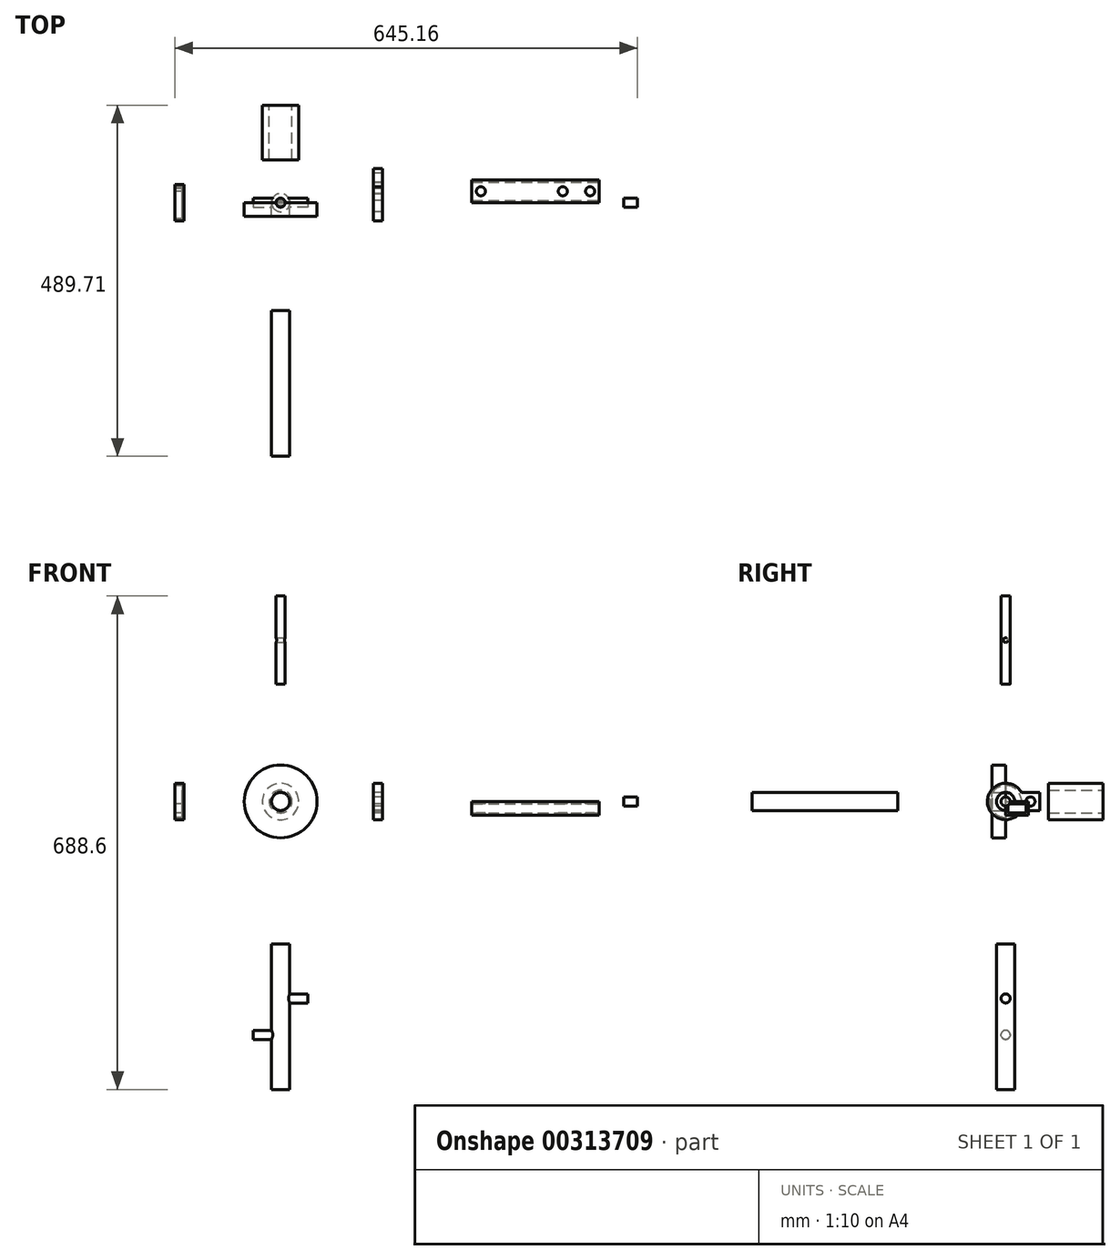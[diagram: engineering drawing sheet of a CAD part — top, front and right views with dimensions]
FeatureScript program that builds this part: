
annotation { "Feature Type Name" : "Feature", "Feature Type Description" : "" }
export const myFeature = defineFeature(function(context is Context, id is Id, definition is map)
    precondition{}
    {
        {
            var Q0;
            Q0=qCreatedBy(makeId("Front.planeOp"),FACE);
            var sketch = newSketch(context, id + "F0", { "sketchPlane" : qUnion([Q0])});
            skCircle(sketch, "E0", {"center": v(0, 0) * mm, "radius": 50.8 * mm});
            skCircle(sketch, "E1", {"center": v(0, 0) * mm, "radius": 12.7 * mm});
            skSolve(sketch);
        }
        {
            var Q0;
            Q0 = qSketchRegion(id + "F0", true);
            extrude(context, id + "F1", {"entities" : qUnion([Q0]), "depth" : 19.05 * mm});
        }
        {
            var Q0;
            Q0=qCreatedBy(makeId("Right.planeOp"),FACE);
            cPlane(context, id + "F2", {"entities" : qUnion([Q0]), "cplaneType" : CPlaneType.OFFSET, "offset" : 147.57 * mm, "oppositeDirection" : true, "width" : 152.4 * mm, "height" : 152.4 * mm});
        }
        {
            var Q0;
            Q0=qCreatedBy(id+"F2.planeOp",FACE);
            var sketch = newSketch(context, id + "F3", { "sketchPlane" : qUnion([Q0])});
            skCircle(sketch, "E2", {"center": v(0, 0) * mm, "radius": 25.4 * mm});
            skCircle(sketch, "E3", {"center": v(0, 0) * mm, "radius": 12.7 * mm});
            skSolve(sketch);
        }
        {
            var Q0;
            Q0 = qSketchRegion(id + "F3", true);
            extrude(context, id + "F4", {"entities" : qUnion([Q0]), "depth" : 12.7 * mm});
        }
        {
            var Q0;
            Q0=makeQuery(id+"F4.opExtrude","CAP_FACE",FACE,{"disambiguationData":[OSD([sQuery(id+"F3.wireOp",EDGE,"E2")])],"isStart":true});
            var sketch = newSketch(context, id + "F5", { "sketchPlane" : qUnion([Q0])});
            skCircle(sketch, "E4", {"center": v(0, 0) * mm, "radius": 22.22 * mm});
            skSolve(sketch);
        }
        {
            var Q0;
            Q0 = qSketchRegion(id + "F5", true);
            extrude(context, id + "F6", {"entities" : qUnion([Q0]), "operationType" : NewBodyOperationType.REMOVE, "oppositeDirection" : true, "depth" : 10.16 * mm});
        }
        {
            var Q0;
            Q0=qCreatedBy(makeId("Right.planeOp"),FACE);
            cPlane(context, id + "F7", {"entities" : qUnion([Q0]), "cplaneType" : CPlaneType.OFFSET, "offset" : 129.29 * mm, "width" : 152.4 * mm, "height" : 152.4 * mm});
        }
        {
            var Q0;
            Q0=qCreatedBy(id+"F7.planeOp",FACE);
            var sketch = newSketch(context, id + "F8", { "sketchPlane" : qUnion([Q0])});
            skCircle(sketch, "E5", {"center": v(0, 0) * mm, "radius": 25.4 * mm});
            skCircle(sketch, "E6", {"center": v(0, 0) * mm, "radius": 12.7 * mm});
            skLineSegment(sketch, "E7", {"start": v(0, 0) * mm, "end": v(52.55, 0) * mm, "construction": true});
            skLineSegment(sketch, "E8", {"start": v(22, 12.7) * mm, "end": v(47.4, 12.7) * mm});
            skLineSegment(sketch, "E9", {"start": v(47.4, 12.7) * mm, "end": v(47.4, 0) * mm});
            skLineSegment(sketch, "E10.MirrorCS", {"start": v(47.4, -12.7) * mm, "end": v(47.4, 0) * mm});
            skLineSegment(sketch, "E11.MirrorCS", {"start": v(22, -12.7) * mm, "end": v(47.4, -12.7) * mm});
            skCircle(sketch, "E12", {"center": v(34.7, 0) * mm, "radius": 6.35 * mm});
            skSolve(sketch);
        }
        {
            var Q0;
            Q0=makeQuery(id+"F8.imprint","IMPRINT",FACE,{"disambiguationData":[TD([[makeQuery(id+"F8.imprint","IMPRINT",EDGE,{"derivedFrom":sQuery(id+"F8.wireOp",EDGE,"E6")}),-1.0]])]});
            var Q1;
            {var subQ1=sQuery(id+"F8.wireOp",EDGE,"E8");Q1=makeQuery(id+"F8.imprint","IMPRINT",FACE,{"disambiguationData":[TD([[makeQuery(id+"F8.imprint","IMPRINT",EDGE,{"derivedFrom":subQ1}),-1.0]])]});}
            extrude(context, id + "F9", {"entities" : qUnion([Q0, Q1]), "depth" : 12.7 * mm});
        }
        {
            var Q0;
            Q0=qCreatedBy(makeId("Front.planeOp"),FACE);
            cPlane(context, id + "F10", {"entities" : qUnion([Q0]), "cplaneType" : CPlaneType.OFFSET, "offset" : 135.89 * mm, "oppositeDirection" : true, "width" : 152.4 * mm, "height" : 152.4 * mm});
        }
        {
            var Q0;
            Q0=qCreatedBy(id+"F10.planeOp",FACE);
            var sketch = newSketch(context, id + "F11", { "sketchPlane" : qUnion([Q0])});
            skCircle(sketch, "E13", {"center": v(0, 0) * mm, "radius": 25.4 * mm});
            skCircle(sketch, "E14", {"center": v(0, 0) * mm, "radius": 15.88 * mm});
            skSolve(sketch);
        }
        {
            var Q0;
            Q0 = qSketchRegion(id + "F11", true);
            extrude(context, id + "F12", {"entities" : qUnion([Q0]), "depth" : 76.2 * mm});
        }
        {
            var Q0;
            Q0=qCreatedBy(makeId("Front.planeOp"),FACE);
            cPlane(context, id + "F13", {"entities" : qUnion([Q0]), "cplaneType" : CPlaneType.OFFSET, "offset" : 150.62 * mm, "width" : 152.4 * mm, "height" : 152.4 * mm});
        }
        {
            var Q0;
            Q0=qCreatedBy(id+"F13.planeOp",FACE);
            var sketch = newSketch(context, id + "F14", { "sketchPlane" : qUnion([Q0])});
            skCircle(sketch, "E15", {"center": v(0, 0) * mm, "radius": 12.7 * mm});
            skSolve(sketch);
        }
        {
            var Q0;
            Q0 = qSketchRegion(id + "F14", true);
            extrude(context, id + "F15", {"entities" : qUnion([Q0]), "depth" : 203.2 * mm});
        }
        {
            var Q0;
            Q0=qCreatedBy(makeId("Top.planeOp"),FACE);
            cPlane(context, id + "F16", {"entities" : qUnion([Q0]), "cplaneType" : CPlaneType.OFFSET, "offset" : 163.58 * mm, "width" : 152.4 * mm, "height" : 152.4 * mm});
        }
        {
            var Q0;
            Q0=qCreatedBy(id+"F16.planeOp",FACE);
            var sketch = newSketch(context, id + "F17", { "sketchPlane" : qUnion([Q0])});
            skCircle(sketch, "E16", {"center": v(0, 0) * mm, "radius": 6.35 * mm});
            skSolve(sketch);
        }
        {
            var Q0;
            Q0 = qSketchRegion(id + "F17", true);
            extrude(context, id + "F18", {"entities" : qUnion([Q0]), "depth" : 123.19 * mm});
        }
        {
            var Q0;
            Q0=qCreatedBy(makeId("Right.planeOp"),FACE);
            var sketch = newSketch(context, id + "F19", { "sketchPlane" : qUnion([Q0])});
            skLineSegment(sketch, "E17", {"start": v(-6.35, 163.58) * mm, "end": v(-6.35, 286.77) * mm});
            skCircle(sketch, "E18", {"center": v(0, 225.17) * mm, "radius": 3.18 * mm});
            skPoint(sketch, "E18.centerSnap0", {"position": v(-6.35, 225.17) * mm});
            skLineSegment(sketch, "E19.0", {"start": v(-6.35, 163.58) * mm, "end": v(6.35, 163.58) * mm});
            skLineSegment(sketch, "E20.0", {"start": v(-6.35, 286.77) * mm, "end": v(6.35, 286.77) * mm});
            skSolve(sketch);
        }
        {
            var Q0;
            Q0 = qSketchRegion(id + "F19", true);
            extrude(context, id + "F20", {"entities" : qUnion([Q0]), "operationType" : NewBodyOperationType.REMOVE, "oppositeDirection" : true, "depth" : 25.4 * mm, "hasSecondDirection" : true, "secondDirectionOppositeDirection" : false, "secondDirectionDepth" : 25.4 * mm});
        }
        {
            var Q0;
            Q0=qCreatedBy(makeId("Top.planeOp"),FACE);
            cPlane(context, id + "F21", {"entities" : qUnion([Q0]), "cplaneType" : CPlaneType.OFFSET, "offset" : 198.63 * mm, "oppositeDirection" : true, "width" : 152.4 * mm, "height" : 152.4 * mm});
        }
        {
            var Q0;
            Q0=qCreatedBy(id+"F21.planeOp",FACE);
            var sketch = newSketch(context, id + "F22", { "sketchPlane" : qUnion([Q0])});
            skCircle(sketch, "E21", {"center": v(0, 0) * mm, "radius": 12.7 * mm});
            skSolve(sketch);
        }
        {
            var Q0;
            Q0=makeQuery(id+"F22.imprint","IMPRINT",FACE,{"disambiguationData":[TD([[makeQuery(id+"F22.imprint","IMPRINT",EDGE,{"derivedFrom":sQuery(id+"F22.wireOp",EDGE,"E21")}),1.0]])]});
            var Q1;
            Q1=sQuery(id+"F22.wireOp",EDGE,"E21");
            extrude(context, id + "F23", {"entities" : qUnion([Q0]), "surfaceEntities" : qUnion([Q1]), "oppositeDirection" : true, "depth" : 203.2 * mm});
        }
        {
            var Q0;
            Q0=qCreatedBy(makeId("Right.planeOp"),FACE);
            var sketch = newSketch(context, id + "F24", { "sketchPlane" : qUnion([Q0])});
            skLineSegment(sketch, "E22.0.0", {"start": v(-12.7, -198.63) * mm, "end": v(12.7, -198.63) * mm});
            skCircle(sketch, "E23", {"center": v(0, -274.83) * mm, "radius": 6.35 * mm});
            skPoint(sketch, "E23.centerSnap0", {"position": v(0, -198.63) * mm});
            skPoint(sketch, "E24.0.0.end.orphan", {"position": v(-12.7, -401.83) * mm});
            skPoint(sketch, "E24.0.0.start.orphan", {"position": v(12.7, -401.83) * mm});
            skCircle(sketch, "E25", {"center": v(0, -325.63) * mm, "radius": 6.35 * mm});
            skSolve(sketch);
        }
        {
            var Q0;
            Q0=makeQuery(id+"F24.imprint","IMPRINT",FACE,{"disambiguationData":[TD([[makeQuery(id+"F24.imprint","IMPRINT",EDGE,{"derivedFrom":sQuery(id+"F24.wireOp",EDGE,"E23")}),1.0]])]});
            extrude(context, id + "F25", {"entities" : qUnion([Q0]), "operationType" : NewBodyOperationType.ADD, "depth" : 38.1 * mm});
        }
        {
            var Q0;
            Q0=makeQuery(id+"F24.imprint","IMPRINT",FACE,{"disambiguationData":[TD([[makeQuery(id+"F24.imprint","IMPRINT",EDGE,{"derivedFrom":sQuery(id+"F24.wireOp",EDGE,"E25")}),1.0]])]});
            extrude(context, id + "F26", {"entities" : qUnion([Q0]), "operationType" : NewBodyOperationType.ADD, "oppositeDirection" : true, "depth" : 38.1 * mm});
        }
        {
            var Q0;
            Q0=qCreatedBy(makeId("Right.planeOp"),FACE);
            cPlane(context, id + "F27", {"entities" : qUnion([Q0]), "cplaneType" : CPlaneType.OFFSET, "offset" : 266.7 * mm, "width" : 152.4 * mm, "height" : 152.4 * mm});
        }
        {
            var Q0;
            Q0=qCreatedBy(id+"F27.planeOp",FACE);
            var sketch = newSketch(context, id + "F28", { "sketchPlane" : qUnion([Q0])});
            skLineSegment(sketch, "E26.bottom", {"start": v(0, 0) * mm, "end": v(31.75, 0) * mm});
            skLineSegment(sketch, "E26.top", {"start": v(0, -19.05) * mm, "end": v(31.75, -19.05) * mm});
            skLineSegment(sketch, "E26.left", {"start": v(0, 0) * mm, "end": v(0, -19.05) * mm});
            skLineSegment(sketch, "E26.right", {"start": v(31.75, 0) * mm, "end": v(31.75, -19.05) * mm});
            skSolve(sketch);
        }
        {
            var Q0;
            Q0=makeQuery(id+"F28.imprint","IMPRINT",FACE,{"disambiguationData":[TD([[makeQuery(id+"F28.imprint","IMPRINT",EDGE,{"derivedFrom":sQuery(id+"F28.wireOp",EDGE,"E26.bottom")}),-1.0]])]});
            extrude(context, id + "F29", {"entities" : qUnion([Q0]), "depth" : 177.8 * mm});
        }
        {
            var Q0;
            Q0=makeQuery(id+"F29.opExtrude","CAP_FACE",FACE,{"disambiguationData":[OSD([sQuery(id+"F28.wireOp",EDGE,"E26.bottom"),sQuery(id+"F28.wireOp",EDGE,"E26.top"),sQuery(id+"F28.wireOp",EDGE,"E26.left"),sQuery(id+"F28.wireOp",EDGE,"E26.right")])],"isStart":false});
            var sketch = newSketch(context, id + "F30", { "sketchPlane" : qUnion([Q0])});
            skLineSegment(sketch, "E27.bottom", {"start": v(28.58, -3.17) * mm, "end": v(3.18, -3.18) * mm});
            skLineSegment(sketch, "E27.top", {"start": v(28.58, -15.88) * mm, "end": v(3.18, -15.88) * mm});
            skLineSegment(sketch, "E27.left", {"start": v(28.58, -3.18) * mm, "end": v(28.58, -15.88) * mm});
            skLineSegment(sketch, "E27.right", {"start": v(3.18, -3.18) * mm, "end": v(3.18, -15.88) * mm});
            skSolve(sketch);
        }
        {
            var Q0;
            Q0 = qSketchRegion(id + "F30", true);
            extrude(context, id + "F31", {"entities" : qUnion([Q0]), "operationType" : NewBodyOperationType.REMOVE, "endBound" : BoundingType.THROUGH_ALL, "oppositeDirection" : true, "depth" : 25.4 * mm});
        }
        {
            var Q0;
            Q0=makeQuery(id+"F29.opExtrude","SWEPT_FACE",FACE,{"disambiguationData":[OSD([sQuery(id+"F28.wireOp",EDGE,"E26.bottom")])]});
            var sketch = newSketch(context, id + "F32", { "sketchPlane" : qUnion([Q0])});
            skCircle(sketch, "E28", {"center": v(279.4, 15.88) * mm, "radius": 6.35 * mm});
            skPoint(sketch, "E28.centerSnap0", {"position": v(266.7, 15.88) * mm});
            skCircle(sketch, "E29", {"center": v(431.8, 15.88) * mm, "radius": 6.35 * mm});
            skCircle(sketch, "E30", {"center": v(393.7, 15.88) * mm, "radius": 6.35 * mm});
            skSolve(sketch);
        }
        {
            var Q0;
            Q0 = qSketchRegion(id + "F32", true);
            extrude(context, id + "F33", {"entities" : qUnion([Q0]), "operationType" : NewBodyOperationType.REMOVE, "endBound" : BoundingType.THROUGH_ALL, "oppositeDirection" : true, "depth" : 25.4 * mm});
        }
        {
            var Q0;
            Q0=qCreatedBy(makeId("Right.planeOp"),FACE);
            cPlane(context, id + "F34", {"entities" : qUnion([Q0]), "cplaneType" : CPlaneType.OFFSET, "offset" : 478.54 * mm, "width" : 152.4 * mm, "height" : 152.4 * mm});
        }
        {
            var Q0;
            Q0=qCreatedBy(id+"F34.planeOp",FACE);
            var sketch = newSketch(context, id + "F35", { "sketchPlane" : qUnion([Q0])});
            skCircle(sketch, "E31", {"center": v(0, 0) * mm, "radius": 6.35 * mm});
            skSolve(sketch);
        }
        {
            var Q0;
            Q0 = qSketchRegion(id + "F35", true);
            extrude(context, id + "F36", {"entities" : qUnion([Q0]), "depth" : 19.05 * mm});
        }
    });
